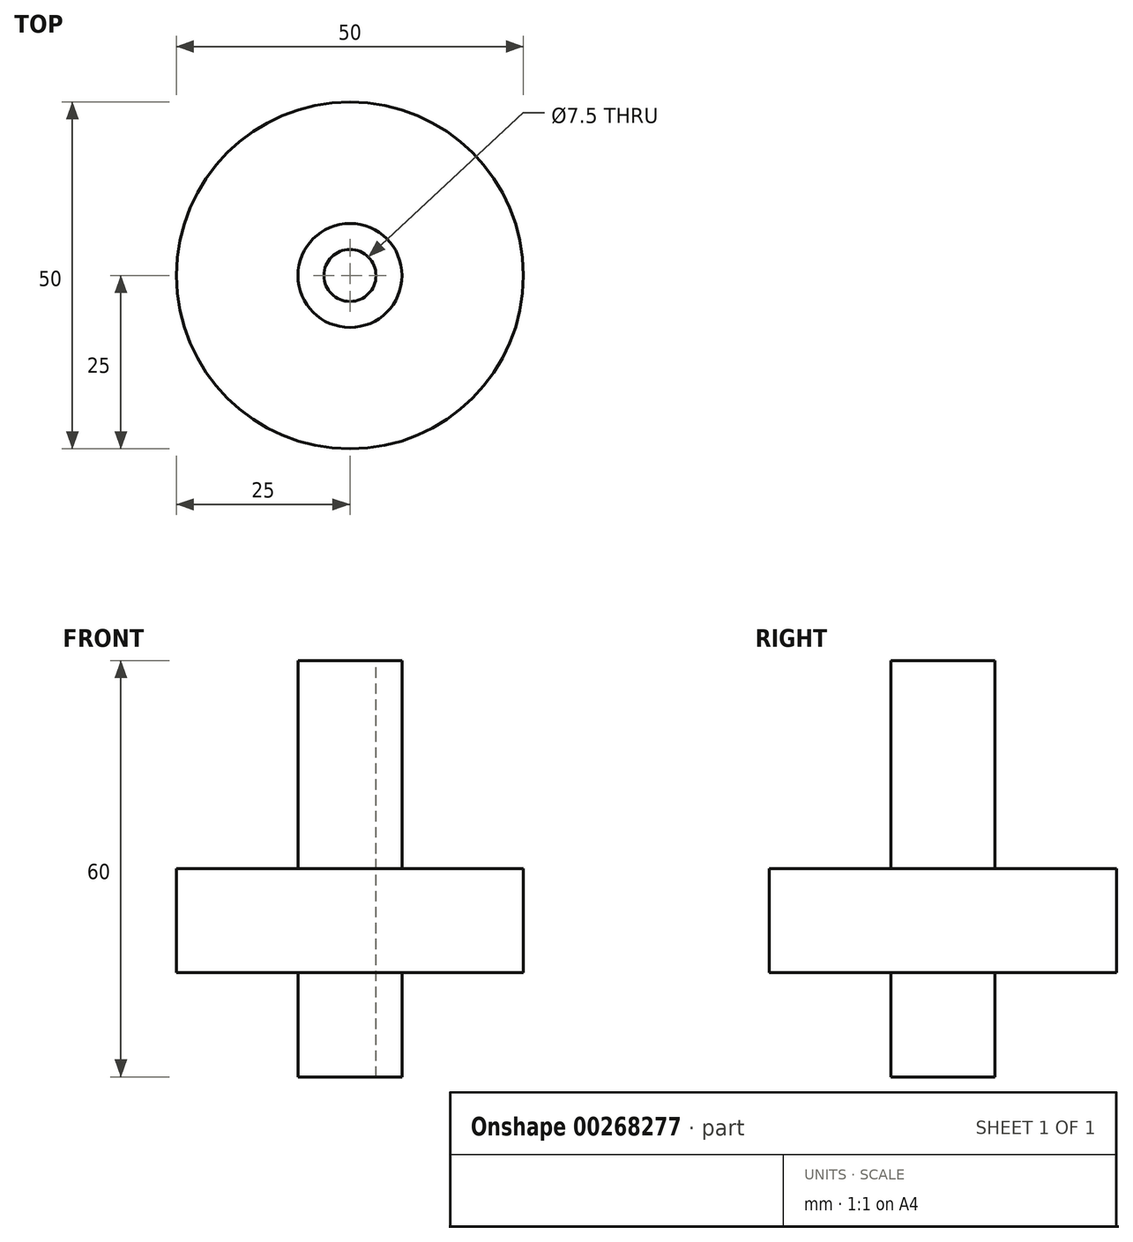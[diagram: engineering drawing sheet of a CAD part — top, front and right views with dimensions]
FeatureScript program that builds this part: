
annotation { "Feature Type Name" : "Feature", "Feature Type Description" : "" }
export const myFeature = defineFeature(function(context is Context, id is Id, definition is map)
    precondition{}
    {
        {
            var Q0;
            Q0=qCreatedBy(makeId("Top.planeOp"),FACE);
            var sketch = newSketch(context, id + "F0", { "sketchPlane" : qUnion([Q0])});
            skCircle(sketch, "E0", {"center": v(0, 0) * mm, "radius": 25 * mm});
            skSolve(sketch);
        }
        {
            var Q0;
            Q0 = qSketchRegion(id + "F0", true);
            extrude(context, id + "F1", {"entities" : qUnion([Q0]), "depth" : 15 * mm});
        }
        {
            var Q0;
            Q0=makeQuery(id+"F1.opExtrude","CAP_FACE",FACE,{"disambiguationData":[OSD([sQuery(id+"F0.wireOp",EDGE,"E0")])],"isStart":false});
            var sketch = newSketch(context, id + "F2", { "sketchPlane" : qUnion([Q0])});
            skCircle(sketch, "E1", {"center": v(0, 0) * mm, "radius": 7.5 * mm});
            skSolve(sketch);
        }
        {
            var Q0;
            Q0 = qSketchRegion(id + "F2", true);
            extrude(context, id + "F3", {"entities" : qUnion([Q0]), "operationType" : NewBodyOperationType.ADD, "depth" : 30 * mm});
        }
        {
            var Q0;
            Q0=makeQuery(id+"F1.opExtrude","CAP_FACE",FACE,{"disambiguationData":[OSD([sQuery(id+"F0.wireOp",EDGE,"E0")])],"isStart":true});
            var sketch = newSketch(context, id + "F4", { "sketchPlane" : qUnion([Q0])});
            skCircle(sketch, "E2", {"center": v(0, 0) * mm, "radius": 7.5 * mm});
            skSolve(sketch);
        }
        {
            var Q0;
            Q0 = qSketchRegion(id + "F4", true);
            extrude(context, id + "F5", {"entities" : qUnion([Q0]), "operationType" : NewBodyOperationType.ADD, "depth" : 15 * mm});
        }
        {
            var Q0;
            Q0=makeQuery(id+"F3.opExtrude","CAP_FACE",FACE,{"disambiguationData":[OSD([sQuery(id+"F2.wireOp",EDGE,"E1")])],"isStart":false});
            var sketch = newSketch(context, id + "F6", { "sketchPlane" : qUnion([Q0])});
            skCircle(sketch, "E3", {"center": v(0, 0) * mm, "radius": 3.75 * mm});
            skSolve(sketch);
        }
        {
            var Q0;
            Q0 = qSketchRegion(id + "F6", true);
            extrude(context, id + "F7", {"entities" : qUnion([Q0]), "operationType" : NewBodyOperationType.REMOVE, "oppositeDirection" : true, "depth" : 113.7 * mm});
        }
    });
